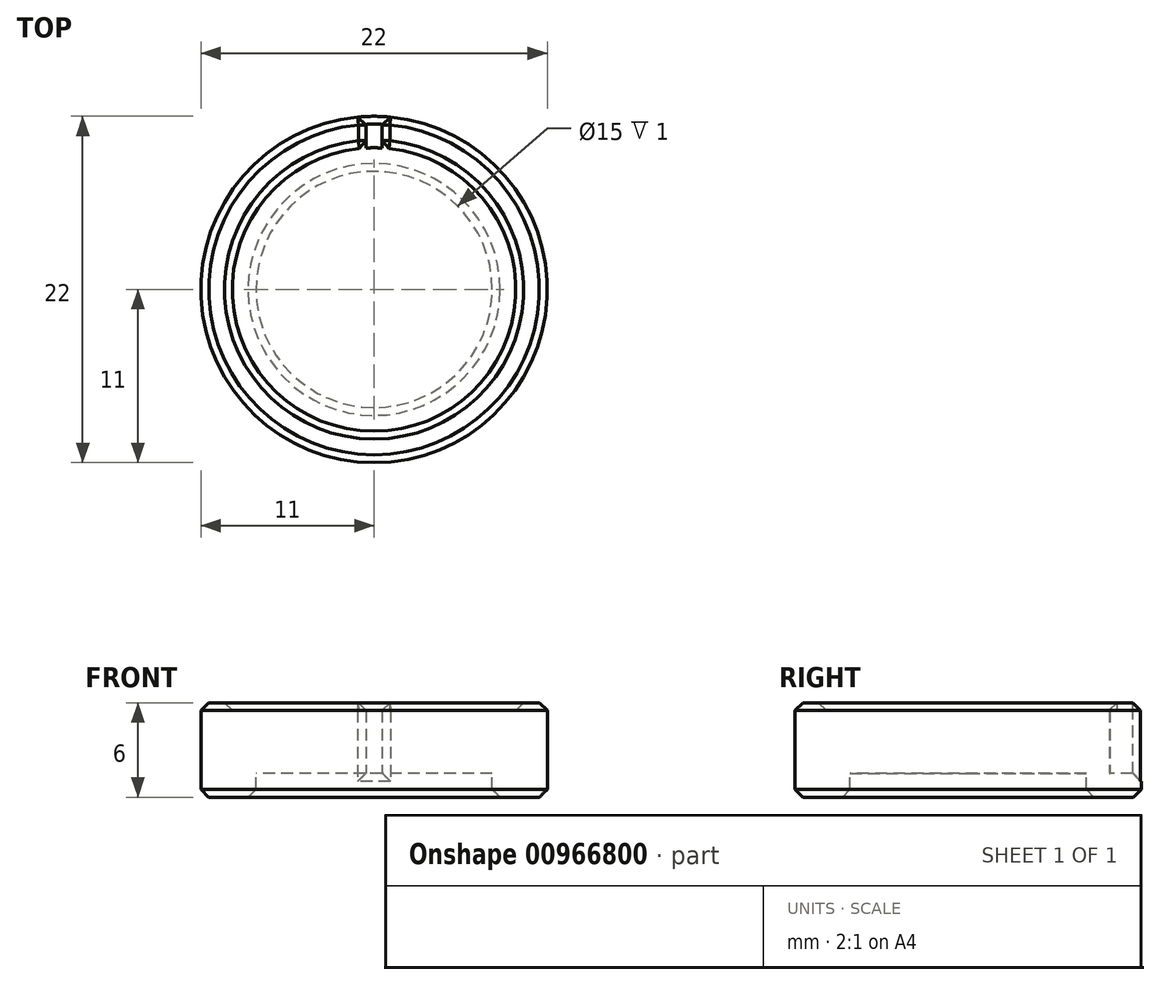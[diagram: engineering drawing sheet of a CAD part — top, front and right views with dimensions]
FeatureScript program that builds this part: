
annotation { "Feature Type Name" : "Feature", "Feature Type Description" : "" }
export const myFeature = defineFeature(function(context is Context, id is Id, definition is map)
    precondition{}
    {
        {
            var Q0;
            Q0=qCreatedBy(makeId("Top.planeOp"),FACE);
            var sketch = newSketch(context, id + "F0", { "sketchPlane" : qUnion([Q0])});
            skCircle(sketch, "E0", {"center": v(0, 0) * mm, "radius": 9 * mm});
            skSolve(sketch);
        }
        {
            var Q0;
            Q0 = qSketchRegion(id + "F0", true);
            extrude(context, id + "F1", {"entities" : qUnion([Q0]), "depth" : 4 * mm, "offsetDistance" : 25 * mm});
        }
        {
            var Q0;
            Q0=qCreatedBy(makeId("Top.planeOp"),FACE);
            var sketch = newSketch(context, id + "F2", { "sketchPlane" : qUnion([Q0])});
            skArc(sketch, "E1", {"start": v(-0.5, 8.99) * mm, "mid": v(0, -9) * mm, "end": v(0.5, 8.99) * mm});
            skCircle(sketch, "E2", {"center": v(0, 0) * mm, "radius": 11 * mm});
            skCircle(sketch, "E3", {"center": v(0, 0) * mm, "radius": 7.5 * mm});
            skLineSegment(sketch, "E4", {"start": v(0.5, 10.99) * mm, "end": v(0.5, 8.99) * mm});
            skLineSegment(sketch, "E5.MirrorCS", {"start": v(-0.5, 10.99) * mm, "end": v(-0.5, 8.99) * mm});
            skSolve(sketch);
        }
        {
            var Q0;
            Q0=makeQuery(id+"F2.imprint","IMPRINT",FACE,{"disambiguationData":[TD([[makeQuery(id+"F2.imprint","IMPRINT",EDGE,{"derivedFrom":sQuery(id+"F2.wireOp",EDGE,"E1")}),-1.0]])]});
            extrude(context, id + "F3", {"entities" : qUnion([Q0]), "depth" : 4.5 * mm, "offsetDistance" : 25 * mm});
        }
        {
            var Q0;
            Q0=makeQuery(id+"F2.imprint","IMPRINT",FACE,{"disambiguationData":[TD([[makeQuery(id+"F2.imprint","IMPRINT",EDGE,{"derivedFrom":sQuery(id+"F2.wireOp",EDGE,"E1")}),1.0]])]});
            var Q1;
            Q1=makeQuery(id+"F2.imprint","IMPRINT",FACE,{"disambiguationData":[TD([[makeQuery(id+"F2.imprint","IMPRINT",EDGE,{"derivedFrom":sQuery(id+"F2.wireOp",EDGE,"E1")}),-1.0]])]});
            extrude(context, id + "F4", {"entities" : qUnion([Q0, Q1]), "operationType" : NewBodyOperationType.ADD, "oppositeDirection" : true, "depth" : 1.5 * mm, "offsetDistance" : 25 * mm});
        }
        {
            var Q0;
            Q0=makeQuery(id+"F3.opExtrude","CAP_FACE",FACE,{"disambiguationData":[OSD([sQuery(id+"F2.wireOp",EDGE,"E1"),sQuery(id+"F2.wireOp",EDGE,"E2"),sQuery(id+"F2.wireOp",EDGE,"E4"),sQuery(id+"F2.wireOp",EDGE,"E5.MirrorCS")])],"isStart":false});
            var Q1;
            Q1=makeQuery(id+"F3.opExtrude","SWEPT_EDGE",EDGE,{"disambiguationData":[OSD([sQuery(id+"F2.wireOp",EDGE,"E1"),sQuery(id+"F2.wireOp",EDGE,"E5.MirrorCS")])]});
            var Q2;
            Q2=makeQuery(id+"F3.opExtrude","SWEPT_EDGE",EDGE,{"disambiguationData":[OSD([sQuery(id+"F2.wireOp",EDGE,"E2"),sQuery(id+"F2.wireOp",EDGE,"E5.MirrorCS")])]});
            var Q3;
            Q3=makeQuery(id+"F3.opExtrude","SWEPT_EDGE",EDGE,{"disambiguationData":[OSD([sQuery(id+"F2.wireOp",EDGE,"E1"),sQuery(id+"F2.wireOp",EDGE,"E4")])]});
            var Q4;
            Q4=makeQuery(id+"F3.opExtrude","SWEPT_EDGE",EDGE,{"disambiguationData":[OSD([sQuery(id+"F2.wireOp",EDGE,"E2"),sQuery(id+"F2.wireOp",EDGE,"E4")])]});
            var Q5;
            Q5=makeQuery(id+"F4.opExtrude","CAP_FACE",FACE,{"disambiguationData":[OSD([sQuery(id+"F2.wireOp",EDGE,"E2"),sQuery(id+"F2.wireOp",EDGE,"E3")])],"isStart":false});
            var Q6;
            Q6=makeQuery(id+"F4.opExtrude","CAP_EDGE",EDGE,{"disambiguationData":[OSD([sQuery(id+"F2.wireOp",EDGE,"E2")])],"isStart":true});
            chamfer(context, id + "F5", {"entities" : qUnion([Q0, Q1, Q2, Q3, Q4, Q5, Q6]), "width" : 0.5 * mm, "tangentPropagation" : true});
        }
    });
